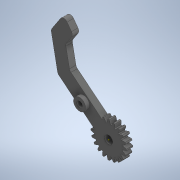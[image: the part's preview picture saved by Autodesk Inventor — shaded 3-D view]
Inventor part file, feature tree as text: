
AUTODESK INVENTOR PART (.ipt)
format: ipt  version: 2021 (Build 250183000, 183)  size: 493,056 bytes
history: native  units: mm
features: sketch x11, extrude x8, other x2
ambient origin geometry x8: Origin, YZ Plane, XZ Plane, XY Plane, X Axis, Y Axis, Z Axis, Center Point
bodies: Solid1 (feature_tree)
feature tree (21):
  extrude  "Extrusion1"  Depth=20.0mm
  extrude  "Extrusion2"  Depth=4.415mm
  extrude  "Extrusion3"  Depth=10.294216mm
  sketch  "Sketch5"  dims[d8=2.5mm d11=11.34mm]
  extrude  "Extrusion4"  Depth=2.5mm
  sketch  "Sketch7"  dims[d16=5.75mm d17=9.873328mm]
  other  "Spur Gear Teeth1"
  extrude  "Extrusion5"  Depth=2.5mm
  extrude  "Extrusion6"  Depth=9.873328mm
  sketch  "Sketch11"  dims[d26=2.5mm]
  extrude  "Extrusion7"  Depth=9.37mm
  extrude  "Extrusion8"  Depth=8.83mm
  sketch  "Sketch1"  dims[d0=5.0mm d1=20.0mm]
  sketch  "Sketch2"  dims[d2=24.631832mm d3=4.415mm]
  sketch  "Sketch4"  dims[d4=28.900907mm d6=10.294216mm]
  sketch  "Sketch6"  dims[d13=17.650515mm d14=2.5mm]
  other  "Spur Gear1"
  sketch  "Sketch9"  dims[d18=2.5mm d22=9.37mm]
  sketch  "Sketch10"  dims[d23=8.3mm d25=8.83mm]
  sketch  "Sketch12"  dims[d27=3.5mm]
  sketch  "Sketch13"  dims[d34=11.05317mm d41=0.5mm d44=170.0mm d46=48.869219mm d48=4.0mm d49=0.0mm d50=7.5mm d51=2.5mm d52=0.0mm d55=21.0mm d56=10.0mm d57=0.0mm d58=22.0mm d59=4.0mm d60=0.0mm d61=4.0mm d62=0.0mm d63=20.0mm d64=24.631832mm d65=3.5mm d66=4.415mm d67=8.83mm d68=22.0mm d69=23.58mm d70=2.5mm d72=11.34mm d73=17.650515mm d74=2.5mm d76=2.452979mm d77=5.75mm d78=9.873328mm d79=2.5mm d80=9.37mm d81=8.3mm d82=2.5mm d83=4.0mm d84=0.0mm d85=7.5mm d86=2.5mm d87=0.0mm d88=12.14051mm d90=2.5mm d91=4.0mm d92=0.0mm]
